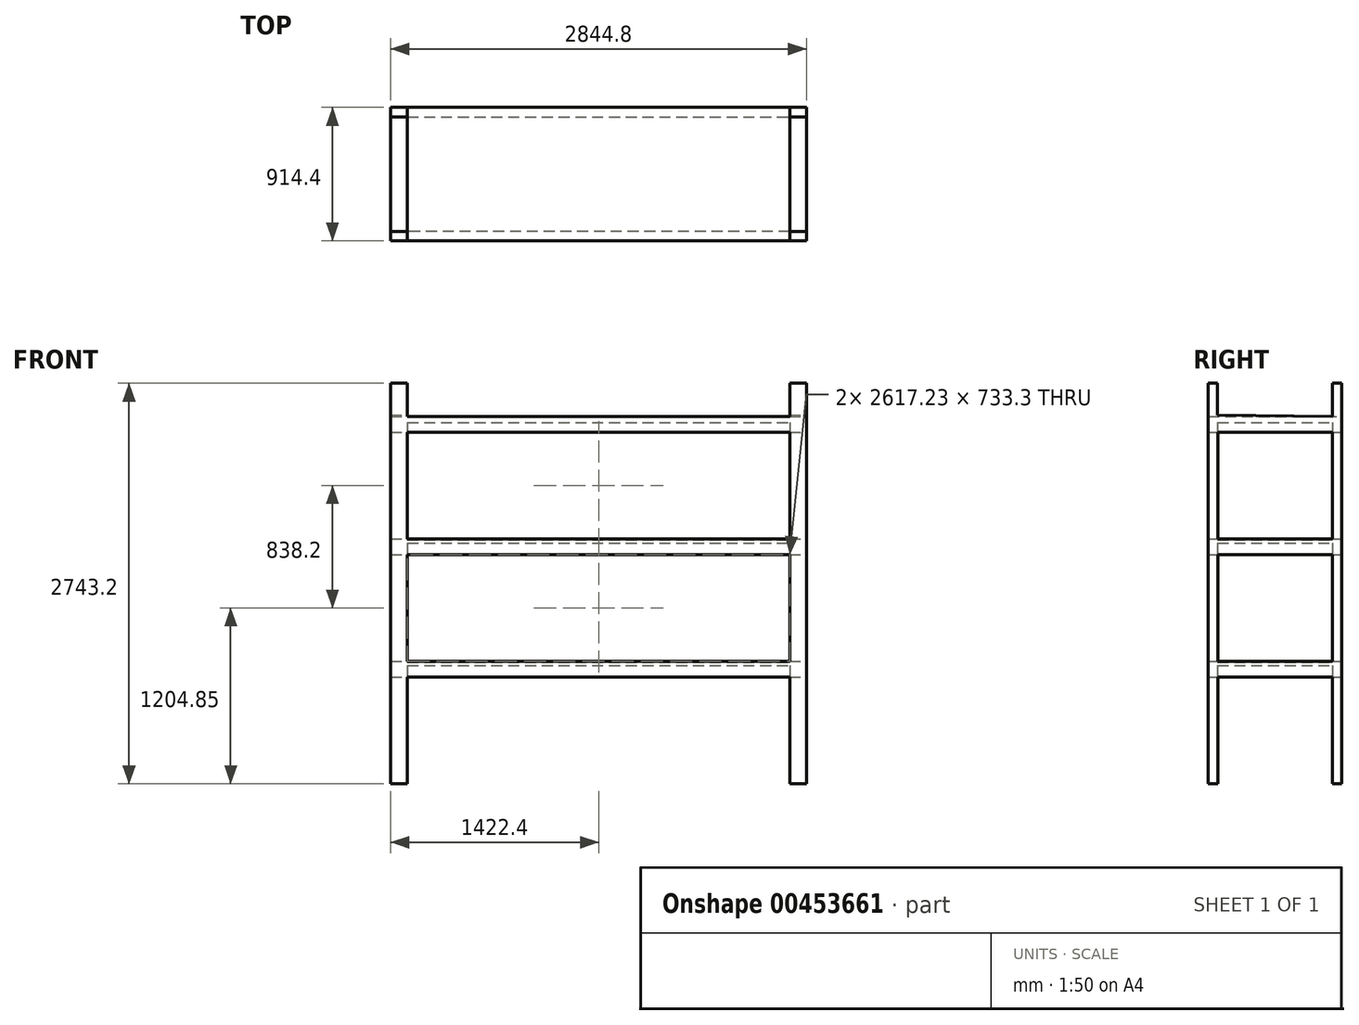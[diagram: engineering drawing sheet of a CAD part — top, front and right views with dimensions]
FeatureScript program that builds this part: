
annotation { "Feature Type Name" : "Feature", "Feature Type Description" : "" }
export const myFeature = defineFeature(function(context is Context, id is Id, definition is map)
    precondition{}
    {
        {
            var Q0;
            Q0=qCreatedBy(makeId("Front.planeOp"),FACE);
            var sketch = newSketch(context, id + "F0", { "sketchPlane" : qUnion([Q0])});
            skLineSegment(sketch, "E0.left", {"start": v(-1366.02, 0) * mm, "end": v(-1366.02, 2743.2) * mm});
            skLineSegment(sketch, "E0.right", {"start": v(1478.78, 0) * mm, "end": v(1478.78, 2743.2) * mm});
            skLineSegment(sketch, "E1.top", {"start": v(-1252.24, 2514.6) * mm, "end": v(1365, 2514.6) * mm});
            skLineSegment(sketch, "E1.left", {"start": v(-1252.24, 2743.2) * mm, "end": v(-1252.24, 2514.6) * mm});
            skLineSegment(sketch, "E1.right", {"start": v(1365, 2743.2) * mm, "end": v(1365, 2514.6) * mm});
            skLineSegment(sketch, "E2", {"start": v(-1366.02, 2743.2) * mm, "end": v(-1252.24, 2743.2) * mm});
            skLineSegment(sketch, "E3", {"start": v(1365, 2743.2) * mm, "end": v(1478.78, 2743.2) * mm});
            skLineSegment(sketch, "E4", {"start": v(-1252.24, 0) * mm, "end": v(-1252.24, 2514.6) * mm});
            skLineSegment(sketch, "E5", {"start": v(1365, 2514.6) * mm, "end": v(1365, 0) * mm});
            skLineSegment(sketch, "E6", {"start": v(-1252.24, 2409.7) * mm, "end": v(1365, 2409.7) * mm});
            skLineSegment(sketch, "E7", {"start": v(-1252.24, 1676.4) * mm, "end": v(1365, 1676.4) * mm});
            skLineSegment(sketch, "E8", {"start": v(-1252.24, 1571.5) * mm, "end": v(1365, 1571.5) * mm});
            skLineSegment(sketch, "E9", {"start": v(-1252.24, 2514.6) * mm, "end": v(-1252.24, 2409.7) * mm});
            skLineSegment(sketch, "E10", {"start": v(1365, 2514.6) * mm, "end": v(1365, 2409.7) * mm});
            skLineSegment(sketch, "E11", {"start": v(1365, 1676.4) * mm, "end": v(1365, 1571.5) * mm});
            skLineSegment(sketch, "E12", {"start": v(-1252.24, 1676.4) * mm, "end": v(-1252.24, 1571.5) * mm});
            skLineSegment(sketch, "E13", {"start": v(-1252.24, 838.2) * mm, "end": v(1365, 838.2) * mm});
            skLineSegment(sketch, "E14", {"start": v(-1252.24, 733.3) * mm, "end": v(1365, 733.3) * mm});
            skLineSegment(sketch, "E15", {"start": v(-1366.02, 0) * mm, "end": v(-1252.24, 0) * mm});
            skLineSegment(sketch, "E16", {"start": v(1365, 0) * mm, "end": v(1478.78, 0) * mm});
            skSolve(sketch);
        }
        {
            var Q0;
            Q0=makeQuery(id+"F0.imprint","IMPRINT",FACE,{"disambiguationData":[TD([[makeQuery(id+"F0.imprint","IMPRINT",EDGE,{"derivedFrom":sQuery(id+"F0.wireOp",EDGE,"E0.left")}),-1.0]])]});
            var Q1;
            Q1=makeQuery(id+"F0.imprint","IMPRINT",FACE,{"disambiguationData":[TD([[makeQuery(id+"F0.imprint","IMPRINT",EDGE,{"derivedFrom":sQuery(id+"F0.wireOp",EDGE,"E1.top")}),-1.0]])]});
            var Q2;
            Q2=makeQuery(id+"F0.imprint","IMPRINT",FACE,{"disambiguationData":[TD([[makeQuery(id+"F0.imprint","IMPRINT",EDGE,{"derivedFrom":sQuery(id+"F0.wireOp",EDGE,"E0.right")}),1.0]])]});
            var Q3;
            Q3=makeQuery(id+"F0.imprint","IMPRINT",FACE,{"disambiguationData":[TD([[makeQuery(id+"F0.imprint","IMPRINT",EDGE,{"derivedFrom":sQuery(id+"F0.wireOp",EDGE,"E7")}),-1.0]])]});
            var Q4;
            {var subQ0=sQuery(id+"F0.wireOp",EDGE,"E13");Q4=makeQuery(id+"F0.imprint","IMPRINT",FACE,{"disambiguationData":[TD([[makeQuery(id+"F0.imprint","IMPRINT",EDGE,{"derivedFrom":subQ0}),-1.0]])]});}
            extrude(context, id + "F1", {"entities" : qUnion([Q0, Q1, Q2, Q3, Q4]), "depth" : 914.4 * mm});
        }
        {
            var Q0;
            {var subQ0=sQuery(id+"F0.wireOp",EDGE,"E4");Q0=makeQuery(id+"F1.opExtrude","SWEPT_FACE",FACE,{"disambiguationData":[OSD([subQ0]),TDD([makeQuery(id+"F0.imprint","IMPRINT",EDGE,{"disambiguationData":[TD([[makeQuery(id+"F0.imprint","INTERSECT",VERTEX,{"derivedFrom":[subQ0,sQuery(id+"F0.wireOp",EDGE,"E13")]}),-1.0]])],"derivedFrom":subQ0})])]});}
            var sketch = newSketch(context, id + "F2", { "sketchPlane" : qUnion([Q0])});
            skLineSegment(sketch, "E17", {"start": v(-849.68, 1676.4) * mm, "end": v(-849.68, 2409.7) * mm});
            skLineSegment(sketch, "E18", {"start": v(-64.72, 2409.7) * mm, "end": v(-64.72, 1676.4) * mm});
            skLineSegment(sketch, "E19", {"start": v(-64.72, 1676.4) * mm, "end": v(0, 1676.4) * mm});
            skLineSegment(sketch, "E20", {"start": v(-849.68, 1676.4) * mm, "end": v(-914.4, 1676.4) * mm});
            skLineSegment(sketch, "E21", {"start": v(-849.68, 2409.7) * mm, "end": v(-914.4, 2409.7) * mm});
            skLineSegment(sketch, "E22", {"start": v(-64.72, 2409.7) * mm, "end": v(0, 2409.7) * mm});
            skLineSegment(sketch, "E23", {"start": v(-849.68, 2409.7) * mm, "end": v(-64.72, 2409.7) * mm});
            skLineSegment(sketch, "E24", {"start": v(-849.68, 1676.4) * mm, "end": v(-64.72, 1676.4) * mm});
            skSolve(sketch);
        }
        {
            var Q0;
            Q0=makeQuery(id+"F2.imprint","IMPRINT",FACE,{"disambiguationData":[TD([[makeQuery(id+"F2.imprint","IMPRINT",EDGE,{"derivedFrom":sQuery(id+"F2.wireOp",EDGE,"E17")}),-1.0]])]});
            extrude(context, id + "F3", {"entities" : qUnion([Q0]), "operationType" : NewBodyOperationType.REMOVE, "endBound" : BoundingType.THROUGH_ALL, "oppositeDirection" : true, "depth" : 25 * mm, "hasSecondDirection" : true, "secondDirectionOppositeDirection" : false, "secondDirectionDepth" : 5040 * mm});
        }
        {
            var Q0;
            {var subQ0=sQuery(id+"F0.wireOp",EDGE,"E4");Q0=makeQuery(id+"F1.opExtrude","SWEPT_FACE",FACE,{"disambiguationData":[OSD([subQ0]),TDD([makeQuery(id+"F0.imprint","IMPRINT",EDGE,{"disambiguationData":[TD([[makeQuery(id+"F0.imprint","INTERSECT",VERTEX,{"derivedFrom":[subQ0,sQuery(id+"F0.wireOp",EDGE,"E15")]}),-1.0]])],"derivedFrom":subQ0})])]});}
            var sketch = newSketch(context, id + "F4", { "sketchPlane" : qUnion([Q0])});
            skLineSegment(sketch, "E25", {"start": v(-849.68, 0) * mm, "end": v(-849.68, 733.3) * mm});
            skLineSegment(sketch, "E26", {"start": v(-64.72, 733.3) * mm, "end": v(-64.72, 0) * mm});
            skLineSegment(sketch, "E27", {"start": v(-64.72, 0) * mm, "end": v(0, 0) * mm});
            skLineSegment(sketch, "E28", {"start": v(-849.68, 0) * mm, "end": v(-914.4, 0) * mm});
            skLineSegment(sketch, "E29", {"start": v(-849.68, 733.3) * mm, "end": v(-914.4, 733.3) * mm});
            skLineSegment(sketch, "E30", {"start": v(-64.72, 733.3) * mm, "end": v(0, 733.3) * mm});
            skLineSegment(sketch, "E31", {"start": v(-849.68, 733.3) * mm, "end": v(-64.72, 733.3) * mm});
            skLineSegment(sketch, "E32", {"start": v(-849.68, 0) * mm, "end": v(-64.72, 0) * mm});
            skSolve(sketch);
        }
        {
            var Q0;
            Q0=makeQuery(id+"F4.imprint","IMPRINT",FACE,{"disambiguationData":[TD([[makeQuery(id+"F4.imprint","IMPRINT",EDGE,{"derivedFrom":sQuery(id+"F4.wireOp",EDGE,"E25")}),-1.0]])]});
            extrude(context, id + "F5", {"entities" : qUnion([Q0]), "operationType" : NewBodyOperationType.REMOVE, "endBound" : BoundingType.THROUGH_ALL, "oppositeDirection" : true, "depth" : 25 * mm, "hasSecondDirection" : true, "secondDirectionOppositeDirection" : false, "secondDirectionDepth" : 3796 * mm});
        }
        {
            var Q0;
            {var subQ0=sQuery(id+"F0.wireOp",EDGE,"E4");Q0=makeQuery(id+"F1.opExtrude","SWEPT_FACE",FACE,{"disambiguationData":[OSD([subQ0]),TDD([makeQuery(id+"F0.imprint","IMPRINT",EDGE,{"disambiguationData":[TD([[makeQuery(id+"F0.imprint","INTERSECT",VERTEX,{"derivedFrom":[subQ0,sQuery(id+"F0.wireOp",EDGE,"E13")]}),-1.0]])],"derivedFrom":subQ0})])]});}
            var sketch = newSketch(context, id + "F6", { "sketchPlane" : qUnion([Q0])});
            skLineSegment(sketch, "E33", {"start": v(-849.68, 838.2) * mm, "end": v(-849.68, 1571.5) * mm});
            skLineSegment(sketch, "E34", {"start": v(-64.72, 1571.5) * mm, "end": v(-64.72, 838.2) * mm});
            skLineSegment(sketch, "E35", {"start": v(-64.72, 838.2) * mm, "end": v(0, 838.2) * mm});
            skLineSegment(sketch, "E36", {"start": v(-849.68, 838.2) * mm, "end": v(-914.4, 838.2) * mm});
            skLineSegment(sketch, "E37", {"start": v(-849.68, 1571.5) * mm, "end": v(-914.4, 1571.5) * mm});
            skLineSegment(sketch, "E38", {"start": v(-64.72, 1571.5) * mm, "end": v(0, 1571.5) * mm});
            skLineSegment(sketch, "E39", {"start": v(-849.68, 1571.5) * mm, "end": v(-64.72, 1571.5) * mm});
            skLineSegment(sketch, "E40", {"start": v(-849.68, 838.2) * mm, "end": v(-64.72, 838.2) * mm});
            skSolve(sketch);
        }
        {
            var Q0;
            Q0=makeQuery(id+"F6.imprint","IMPRINT",FACE,{"disambiguationData":[TD([[makeQuery(id+"F6.imprint","IMPRINT",EDGE,{"derivedFrom":sQuery(id+"F6.wireOp",EDGE,"E33")}),-1.0]])]});
            extrude(context, id + "F7", {"entities" : qUnion([Q0]), "operationType" : NewBodyOperationType.REMOVE, "endBound" : BoundingType.THROUGH_ALL, "oppositeDirection" : true, "depth" : 25 * mm, "hasSecondDirection" : true, "secondDirectionOppositeDirection" : false, "secondDirectionDepth" : 4910 * mm});
        }
        {
            var Q0;
            Q0=makeQuery(id+"F1.opExtrude","SWEPT_FACE",FACE,{"disambiguationData":[OSD([sQuery(id+"F0.wireOp",EDGE,"E1.left")])]});
            var sketch = newSketch(context, id + "F8", { "sketchPlane" : qUnion([Q0])});
            skLineSegment(sketch, "E41", {"start": v(-850.39, 2524.66) * mm, "end": v(-850.39, 2743.2) * mm});
            skLineSegment(sketch, "E42", {"start": v(-64.65, 2743.2) * mm, "end": v(-64.65, 2514.65) * mm});
            skLineSegment(sketch, "E43", {"start": v(-64.65, 2514.65) * mm, "end": v(0.07, 2514.65) * mm});
            skLineSegment(sketch, "E44", {"start": v(-850.39, 2524.66) * mm, "end": v(-914.33, 2514.65) * mm});
            skLineSegment(sketch, "E45", {"start": v(-850.39, 2743.2) * mm, "end": v(-914.4, 2743.2) * mm});
            skLineSegment(sketch, "E46", {"start": v(-64.65, 2743.2) * mm, "end": v(0, 2743.2) * mm});
            skLineSegment(sketch, "E47", {"start": v(-850.39, 2743.2) * mm, "end": v(-64.65, 2743.2) * mm});
            skLineSegment(sketch, "E48", {"start": v(-850.39, 2524.66) * mm, "end": v(-64.65, 2514.65) * mm});
            skSolve(sketch);
        }
        {
            var Q0;
            Q0=makeQuery(id+"F8.imprint","IMPRINT",FACE,{"disambiguationData":[TD([[makeQuery(id+"F8.imprint","IMPRINT",EDGE,{"derivedFrom":sQuery(id+"F8.wireOp",EDGE,"E41")}),-1.0]])]});
            extrude(context, id + "F9", {"entities" : qUnion([Q0]), "operationType" : NewBodyOperationType.REMOVE, "oppositeDirection" : true, "depth" : 650 * mm, "hasSecondDirection" : true, "secondDirectionOppositeDirection" : false, "secondDirectionDepth" : 3377 * mm});
        }
        {
            var Q0;
            Q0=makeQuery(id+"F3.boolean.opBoolean","MERGE",FACE,{"derivedFrom":[makeQuery(id+"F1.opExtrude","SWEPT_FACE",FACE,{"disambiguationData":[OSD([sQuery(id+"F0.wireOp",EDGE,"E6")])]}),makeQuery(id+"F3.opExtrude","SWEPT_FACE",FACE,{"disambiguationData":[OSD([sQuery(id+"F2.wireOp",EDGE,"E23")])]})]});
            var sketch = newSketch(context, id + "F10", { "sketchPlane" : qUnion([Q0])});
            skLineSegment(sketch, "E49", {"start": v(-1252.24, 850.48) * mm, "end": v(1365, 850.48) * mm});
            skLineSegment(sketch, "E50", {"start": v(1365, 850.48) * mm, "end": v(1365, 63.92) * mm});
            skLineSegment(sketch, "E51", {"start": v(1365, 63.92) * mm, "end": v(-1252.24, 63.92) * mm});
            skLineSegment(sketch, "E52", {"start": v(-1252.24, 63.92) * mm, "end": v(-1252.24, 850.48) * mm});
            skSolve(sketch);
        }
        {
            var Q0;
            {var subQ34=sQuery(id+"F10.wireOp",EDGE,"E49");Q0=makeQuery(id+"F10.imprint","IMPRINT",FACE,{"disambiguationData":[TD([[makeQuery(id+"F10.imprint","IMPRINT",EDGE,{"derivedFrom":subQ34}),-1.0]])]});}
            var Q1;
            Q1=sQuery(id+"F10.wireOp",EDGE,"E49");
            var Q2;
            Q2=sQuery(id+"F10.wireOp",EDGE,"E50");
            var Q3;
            Q3=sQuery(id+"F10.wireOp",EDGE,"E51");
            var Q4;
            Q4=sQuery(id+"F10.wireOp",EDGE,"E52");
            extrude(context, id + "F11", {"entities" : qUnion([Q0]), "operationType" : NewBodyOperationType.REMOVE, "surfaceEntities" : qUnion([Q1, Q2, Q3, Q4]), "oppositeDirection" : true, "depth" : 66 * mm});
        }
        {
            var Q0;
            Q0=makeQuery(id+"F7.boolean.opBoolean","MERGE",FACE,{"derivedFrom":[makeQuery(id+"F1.opExtrude","SWEPT_FACE",FACE,{"disambiguationData":[OSD([sQuery(id+"F0.wireOp",EDGE,"E8")])]}),makeQuery(id+"F7.opExtrude","SWEPT_FACE",FACE,{"disambiguationData":[OSD([sQuery(id+"F6.wireOp",EDGE,"E39")])]})]});
            var sketch = newSketch(context, id + "F12", { "sketchPlane" : qUnion([Q0])});
            skLineSegment(sketch, "E53", {"start": v(-1252.24, 850.48) * mm, "end": v(1365, 850.48) * mm});
            skLineSegment(sketch, "E54", {"start": v(1365, 850.48) * mm, "end": v(1365, 63.92) * mm});
            skLineSegment(sketch, "E55", {"start": v(1365, 63.92) * mm, "end": v(-1252.24, 63.92) * mm});
            skLineSegment(sketch, "E56", {"start": v(-1252.24, 63.92) * mm, "end": v(-1252.24, 850.48) * mm});
            skSolve(sketch);
        }
        {
            var Q0;
            {var subQ34=sQuery(id+"F12.wireOp",EDGE,"E53");Q0=makeQuery(id+"F12.imprint","IMPRINT",FACE,{"disambiguationData":[TD([[makeQuery(id+"F12.imprint","IMPRINT",EDGE,{"derivedFrom":subQ34}),-1.0]])]});}
            extrude(context, id + "F13", {"entities" : qUnion([Q0]), "operationType" : NewBodyOperationType.REMOVE, "oppositeDirection" : true, "depth" : 77 * mm});
        }
        {
            var Q0;
            Q0=makeQuery(id+"F5.boolean.opBoolean","MERGE",FACE,{"derivedFrom":[makeQuery(id+"F1.opExtrude","SWEPT_FACE",FACE,{"disambiguationData":[OSD([sQuery(id+"F0.wireOp",EDGE,"E14")])]}),makeQuery(id+"F5.opExtrude","SWEPT_FACE",FACE,{"disambiguationData":[OSD([sQuery(id+"F4.wireOp",EDGE,"E31")])]})]});
            var sketch = newSketch(context, id + "F14", { "sketchPlane" : qUnion([Q0])});
            skLineSegment(sketch, "E57", {"start": v(-1252.24, 850.48) * mm, "end": v(1365, 850.48) * mm});
            skLineSegment(sketch, "E58", {"start": v(1365, 850.48) * mm, "end": v(1365, 63.92) * mm});
            skLineSegment(sketch, "E59", {"start": v(1365, 63.92) * mm, "end": v(-1252.24, 63.92) * mm});
            skLineSegment(sketch, "E60", {"start": v(-1252.24, 63.92) * mm, "end": v(-1252.24, 850.48) * mm});
            skSolve(sketch);
        }
        {
            var Q0;
            {var subQ33=sQuery(id+"F14.wireOp",EDGE,"E57");Q0=makeQuery(id+"F14.imprint","IMPRINT",FACE,{"disambiguationData":[TD([[makeQuery(id+"F14.imprint","IMPRINT",EDGE,{"derivedFrom":subQ33}),-1.0]])]});}
            var Q1;
            Q1=makeQuery(id+"F3.boolean.opBoolean","MERGE",FACE,{"derivedFrom":[makeQuery(id+"F1.opExtrude","SWEPT_FACE",FACE,{"disambiguationData":[OSD([sQuery(id+"F0.wireOp",EDGE,"E7")])]}),makeQuery(id+"F3.opExtrude","SWEPT_FACE",FACE,{"disambiguationData":[OSD([sQuery(id+"F2.wireOp",EDGE,"E24")])]})]});
            extrude(context, id + "F15", {"entities" : qUnion([Q0, Q1]), "operationType" : NewBodyOperationType.REMOVE, "oppositeDirection" : true, "depth" : 77 * mm});
        }
        {
            var Q0;
            Q0=makeQuery(id+"F3.boolean.opBoolean","MERGE",FACE,{"derivedFrom":[makeQuery(id+"F1.opExtrude","SWEPT_FACE",FACE,{"disambiguationData":[OSD([sQuery(id+"F0.wireOp",EDGE,"E7")])]}),makeQuery(id+"F3.opExtrude","SWEPT_FACE",FACE,{"disambiguationData":[OSD([sQuery(id+"F2.wireOp",EDGE,"E24")])]})]});
            var sketch = newSketch(context, id + "F16", { "sketchPlane" : qUnion([Q0])});
            skLineSegment(sketch, "E61", {"start": v(-1252.24, -63.92) * mm, "end": v(1365, -63.92) * mm});
            skLineSegment(sketch, "E62", {"start": v(1365, -63.92) * mm, "end": v(1365, -850.48) * mm});
            skLineSegment(sketch, "E63", {"start": v(1365, -850.48) * mm, "end": v(-1252.24, -850.48) * mm});
            skLineSegment(sketch, "E64", {"start": v(-1252.24, -850.48) * mm, "end": v(-1252.24, -63.92) * mm});
            skSolve(sketch);
        }
        {
            var Q0;
            {var subQ15=sQuery(id+"F16.wireOp",EDGE,"E61");Q0=makeQuery(id+"F16.imprint","IMPRINT",FACE,{"disambiguationData":[TD([[makeQuery(id+"F16.imprint","IMPRINT",EDGE,{"derivedFrom":subQ15}),-1.0]])]});}
            var Q1;
            Q1=sQuery(id+"F16.wireOp",EDGE,"E61");
            var Q2;
            Q2=sQuery(id+"F16.wireOp",EDGE,"E62");
            var Q3;
            Q3=sQuery(id+"F16.wireOp",EDGE,"E63");
            var Q4;
            Q4=sQuery(id+"F16.wireOp",EDGE,"E64");
            extrude(context, id + "F17", {"entities" : qUnion([Q0]), "operationType" : NewBodyOperationType.REMOVE, "surfaceEntities" : qUnion([Q1, Q2, Q3, Q4]), "oppositeDirection" : true, "depth" : 5 * mm});
        }
        {
            var Q0;
            Q0=makeQuery(id+"F7.boolean.opBoolean","MERGE",FACE,{"derivedFrom":[makeQuery(id+"F1.opExtrude","SWEPT_FACE",FACE,{"disambiguationData":[OSD([sQuery(id+"F0.wireOp",EDGE,"E13")])]}),makeQuery(id+"F7.opExtrude","SWEPT_FACE",FACE,{"disambiguationData":[OSD([sQuery(id+"F6.wireOp",EDGE,"E40")])]})]});
            var sketch = newSketch(context, id + "F18", { "sketchPlane" : qUnion([Q0])});
            skLineSegment(sketch, "E65", {"start": v(-1252.24, -63.92) * mm, "end": v(1365, -63.92) * mm});
            skLineSegment(sketch, "E66", {"start": v(1365, -63.92) * mm, "end": v(1365, -850.48) * mm});
            skLineSegment(sketch, "E67", {"start": v(1365, -850.48) * mm, "end": v(-1252.24, -850.48) * mm});
            skLineSegment(sketch, "E68", {"start": v(-1252.24, -850.48) * mm, "end": v(-1252.24, -63.92) * mm});
            skSolve(sketch);
        }
        {
            var Q0;
            {var subQ14=sQuery(id+"F18.wireOp",EDGE,"E65");Q0=makeQuery(id+"F18.imprint","IMPRINT",FACE,{"disambiguationData":[TD([[makeQuery(id+"F18.imprint","IMPRINT",EDGE,{"derivedFrom":subQ14}),-1.0]])]});}
            extrude(context, id + "F19", {"entities" : qUnion([Q0]), "operationType" : NewBodyOperationType.REMOVE, "oppositeDirection" : true, "depth" : 5 * mm});
        }
    });
